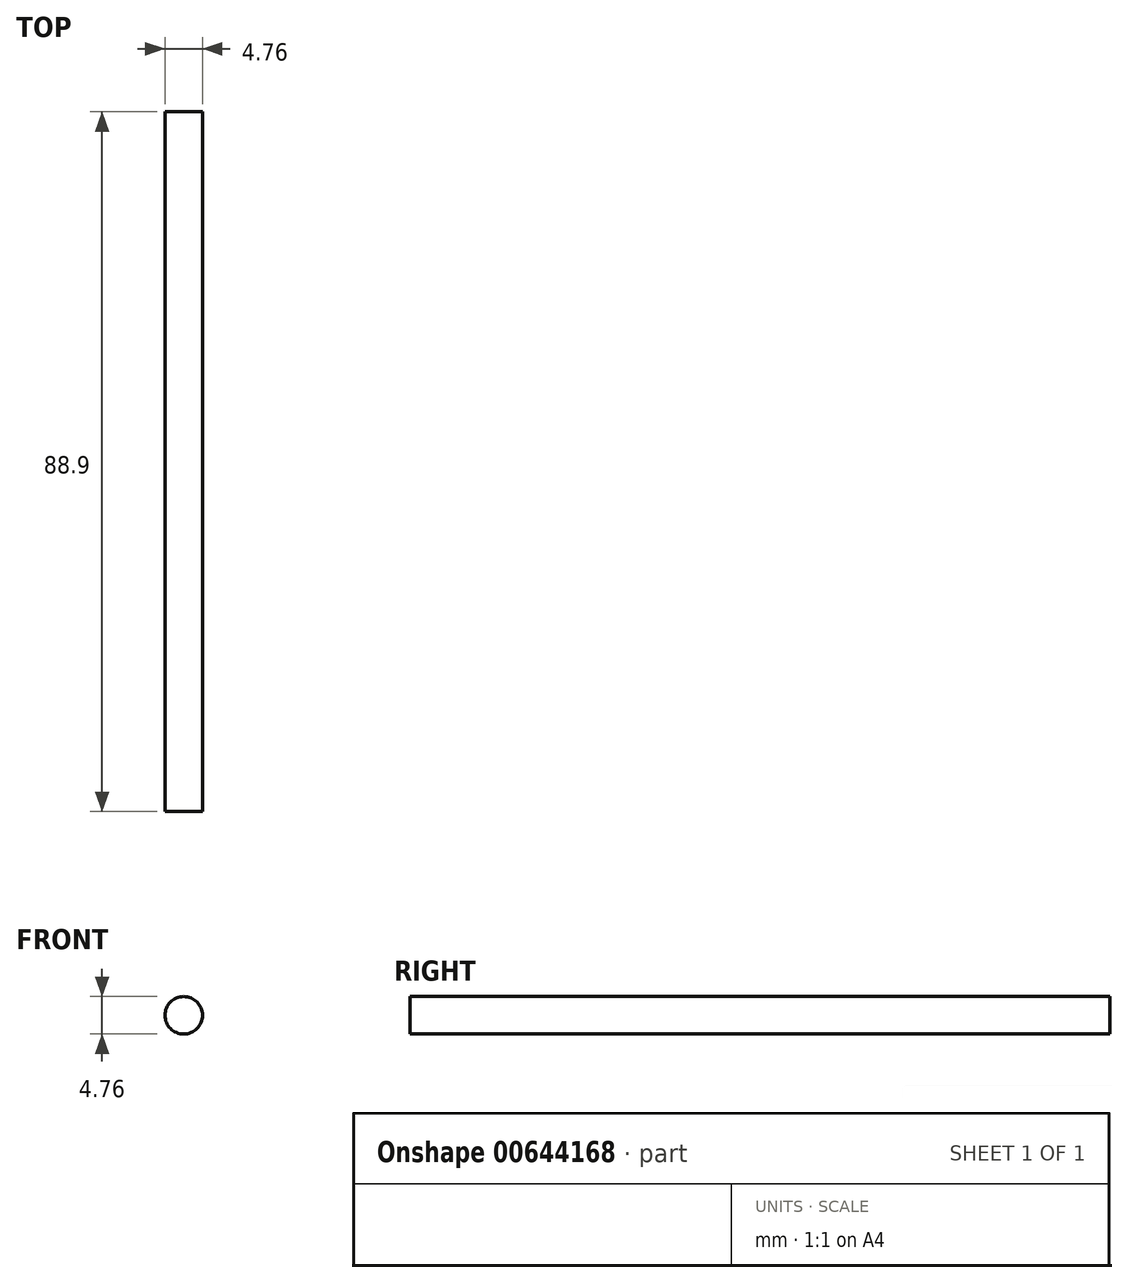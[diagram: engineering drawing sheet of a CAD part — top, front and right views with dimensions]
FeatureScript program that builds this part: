
annotation { "Feature Type Name" : "Feature", "Feature Type Description" : "" }
export const myFeature = defineFeature(function(context is Context, id is Id, definition is map)
    precondition{}
    {
        {
            var Q0;
            Q0=qCreatedBy(makeId("Front.planeOp"),FACE);
            var sketch = newSketch(context, id + "F0", { "sketchPlane" : qUnion([Q0])});
            skCircle(sketch, "E0", {"center": v(0, 0) * mm, "radius": 2.38 * mm});
            skSolve(sketch);
        }
        {
            var Q0;
            Q0 = qSketchRegion(id + "F0", true);
            extrude(context, id + "F1", {"entities" : qUnion([Q0]), "depth" : 88.9 * mm, "offsetDistance" : 25.4 * mm});
        }
    });
